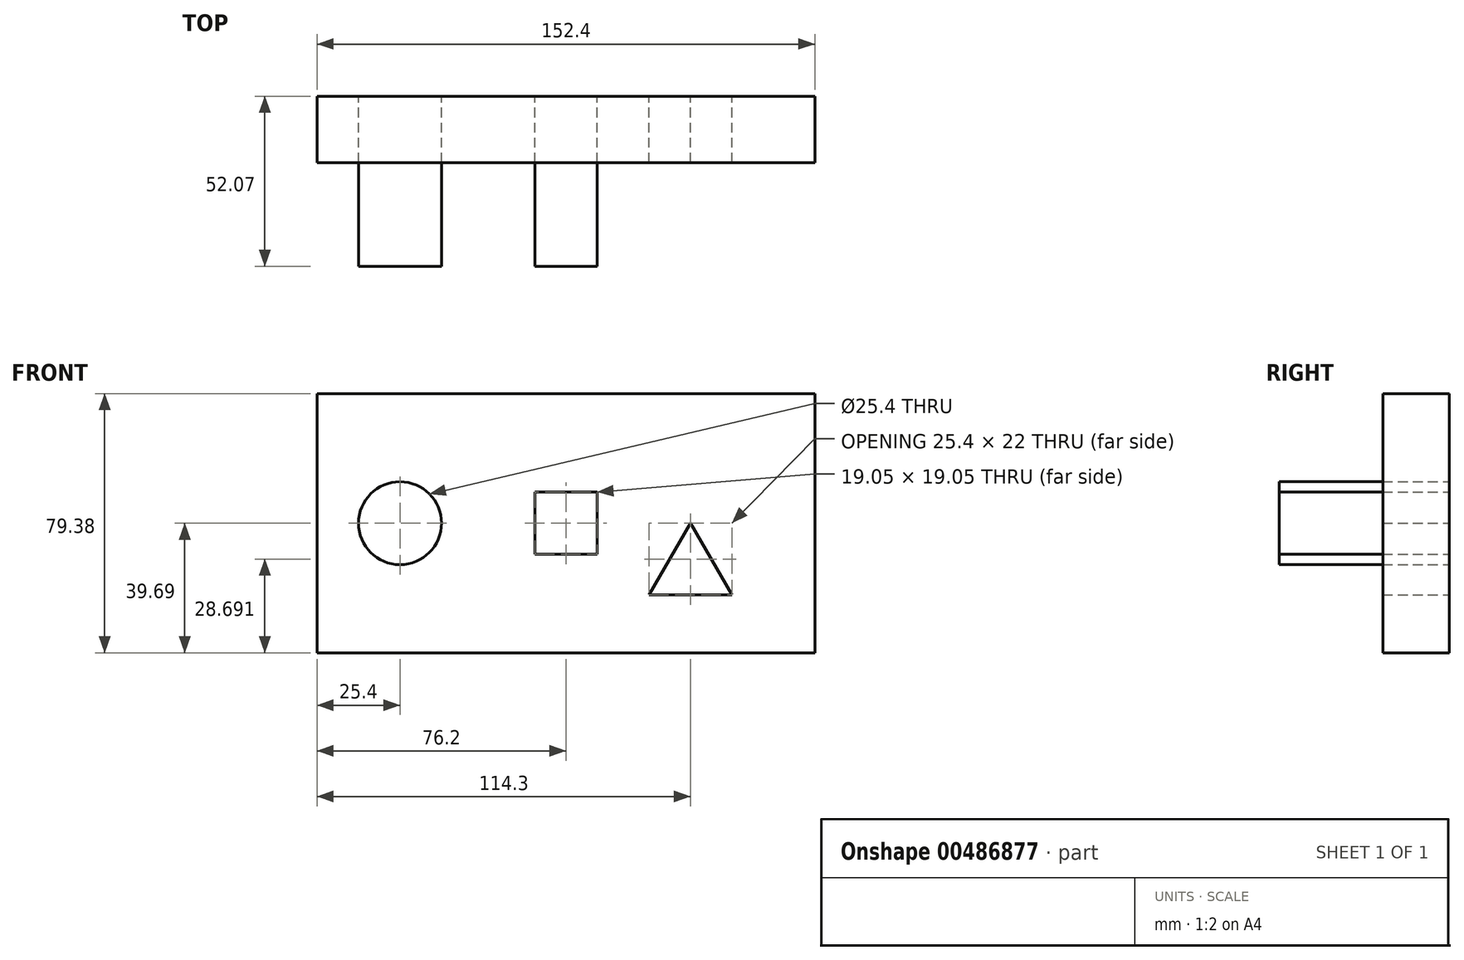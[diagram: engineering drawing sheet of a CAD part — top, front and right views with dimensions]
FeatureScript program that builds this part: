
annotation { "Feature Type Name" : "Feature", "Feature Type Description" : "" }
export const myFeature = defineFeature(function(context is Context, id is Id, definition is map)
    precondition{}
    {
        {
            var Q0;
            Q0=qCreatedBy(makeId("Front.planeOp"),FACE);
            var sketch = newSketch(context, id + "F0", { "sketchPlane" : qUnion([Q0])});
            skLineSegment(sketch, "E0.bottom", {"start": v(-107.95, -39.69) * mm, "end": v(44.45, -39.69) * mm});
            skLineSegment(sketch, "E0.top", {"start": v(-107.95, 39.69) * mm, "end": v(44.45, 39.69) * mm});
            skLineSegment(sketch, "E0.left", {"start": v(-107.95, -39.69) * mm, "end": v(-107.95, 39.69) * mm});
            skLineSegment(sketch, "E0.right", {"start": v(44.45, -39.69) * mm, "end": v(44.45, 39.69) * mm});
            skLineSegment(sketch, "E1", {"start": v(0, 0) * mm, "end": v(0, -39.69) * mm});
            skLineSegment(sketch, "E2.bottom", {"start": v(-22.22, -9.52) * mm, "end": v(-41.28, -9.52) * mm});
            skLineSegment(sketch, "E2.top", {"start": v(-22.23, 9.53) * mm, "end": v(-41.28, 9.53) * mm});
            skLineSegment(sketch, "E2.left", {"start": v(-22.22, -9.52) * mm, "end": v(-22.23, 9.53) * mm});
            skLineSegment(sketch, "E2.right", {"start": v(-41.28, -9.52) * mm, "end": v(-41.28, 9.53) * mm});
            skPoint(sketch, "E2.middle", {"position": v(-31.75, 0) * mm});
            skCircle(sketch, "E3", {"center": v(-82.55, 0) * mm, "radius": 12.7 * mm});
            skLineSegment(sketch, "E4", {"start": v(6.35, 0) * mm, "end": v(-6.35, -22) * mm});
            skLineSegment(sketch, "E5", {"start": v(-6.35, -22) * mm, "end": v(19.05, -22) * mm});
            skLineSegment(sketch, "E6", {"start": v(19.05, -22) * mm, "end": v(6.35, 0) * mm});
            skSolve(sketch);
        }
        {
            var Q0;
            Q0=makeQuery(id+"F0.imprint","IMPRINT",FACE,{"disambiguationData":[TD([[makeQuery(id+"F0.imprint","IMPRINT",EDGE,{"derivedFrom":sQuery(id+"F0.wireOp",EDGE,"E0.top")}),-1.0]])]});
            extrude(context, id + "F1", {"entities" : qUnion([Q0]), "depth" : 20.32 * mm});
        }
        {
            var Q0;
            Q0=makeQuery(id+"F0.imprint","IMPRINT",FACE,{"disambiguationData":[TD([[makeQuery(id+"F0.imprint","IMPRINT",EDGE,{"derivedFrom":sQuery(id+"F0.wireOp",EDGE,"E3")}),1.0]])]});
            extrude(context, id + "F2", {"entities" : qUnion([Q0]), "depth" : 52.07 * mm});
        }
        {
            var Q0;
            Q0=makeQuery(id+"F1.opExtrude","CAP_FACE",FACE,{"disambiguationData":[OSD([sQuery(id+"F0.wireOp",EDGE,"E0.bottom"),sQuery(id+"F0.wireOp",EDGE,"E0.top"),sQuery(id+"F0.wireOp",EDGE,"E0.left"),sQuery(id+"F0.wireOp",EDGE,"E0.right"),sQuery(id+"F0.wireOp",EDGE,"E2.bottom"),sQuery(id+"F0.wireOp",EDGE,"E2.top"),sQuery(id+"F0.wireOp",EDGE,"E2.left"),sQuery(id+"F0.wireOp",EDGE,"E2.right"),sQuery(id+"F0.wireOp",EDGE,"E3"),sQuery(id+"F0.wireOp",EDGE,"E4"),sQuery(id+"F0.wireOp",EDGE,"E5"),sQuery(id+"F0.wireOp",EDGE,"E6")])],"isStart":false});
            var sketch = newSketch(context, id + "F3", { "sketchPlane" : qUnion([Q0])});
            skLineSegment(sketch, "E7.bottom", {"start": v(-107.95, -39.69) * mm, "end": v(44.45, -39.69) * mm});
            skLineSegment(sketch, "E7.top", {"start": v(-107.95, 39.69) * mm, "end": v(44.45, 39.69) * mm});
            skLineSegment(sketch, "E7.left", {"start": v(-107.95, -39.69) * mm, "end": v(-107.95, 39.69) * mm});
            skLineSegment(sketch, "E7.right", {"start": v(44.45, -39.69) * mm, "end": v(44.45, 39.69) * mm});
            skLineSegment(sketch, "E8", {"start": v(-41.28, -9.52) * mm, "end": v(-41.28, 9.53) * mm});
            skLineSegment(sketch, "E9", {"start": v(-41.28, 9.53) * mm, "end": v(-22.23, 9.53) * mm});
            skLineSegment(sketch, "E10", {"start": v(-22.23, 9.53) * mm, "end": v(-22.23, -9.52) * mm});
            skLineSegment(sketch, "E11", {"start": v(-22.23, -9.52) * mm, "end": v(-41.28, -9.52) * mm});
            skSolve(sketch);
        }
        {
            var Q0;
            Q0=makeQuery(id+"F3.imprint","IMPRINT",FACE,{"disambiguationData":[TD([[makeQuery(id+"F3.imprint","IMPRINT",EDGE,{"derivedFrom":sQuery(id+"F3.wireOp",EDGE,"E8")}),-1.0]])]});
            extrude(context, id + "F4", {"entities" : qUnion([Q0]), "depth" : 31.75 * mm});
        }
    });
